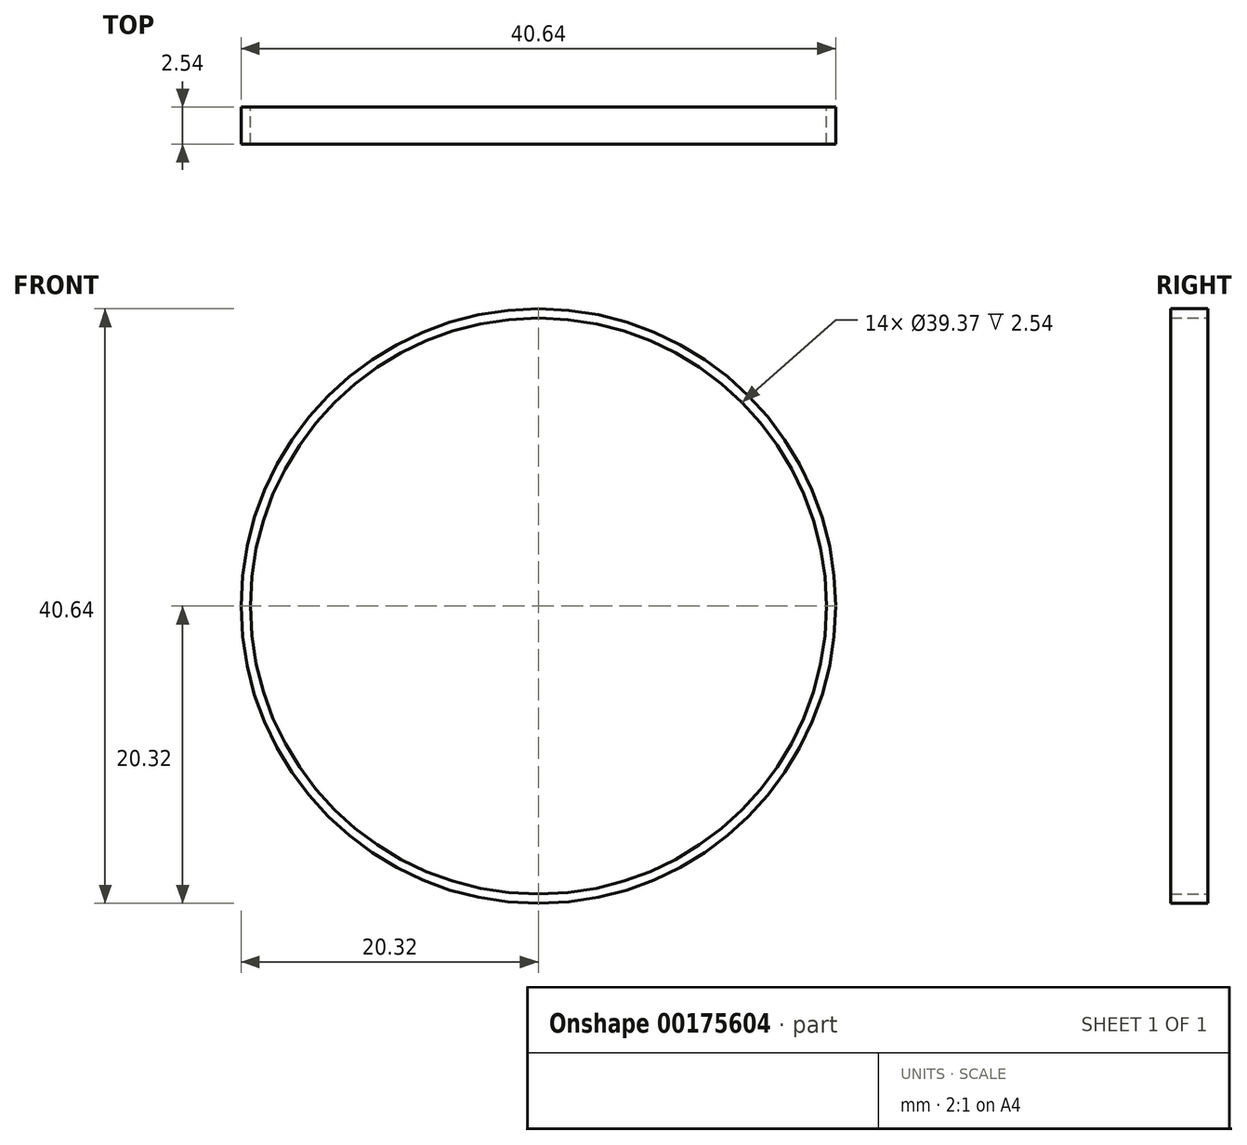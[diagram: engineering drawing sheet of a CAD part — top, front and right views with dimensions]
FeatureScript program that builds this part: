
annotation { "Feature Type Name" : "Feature", "Feature Type Description" : "" }
export const myFeature = defineFeature(function(context is Context, id is Id, definition is map)
    precondition{}
    {
        {
            var Q0;
            Q0=qCreatedBy(makeId("Front.planeOp"),FACE);
            var sketch = newSketch(context, id + "F0", { "sketchPlane" : qUnion([Q0])});
            skCircle(sketch, "E0", {"center": v(0, 0) * mm, "radius": 20.32 * mm});
            skCircle(sketch, "E1", {"center": v(0, 0) * mm, "radius": 19.69 * mm});
            skSolve(sketch);
        }
        {
            var Q0;
            Q0=makeQuery(id+"F0.imprint","IMPRINT",FACE,{"disambiguationData":[TD([[makeQuery(id+"F0.imprint","IMPRINT",EDGE,{"derivedFrom":sQuery(id+"F0.wireOp",EDGE,"E0")}),1.0]])]});
            extrude(context, id + "F1", {"entities" : qUnion([Q0]), "depth" : 2.54 * mm});
        }
    });
